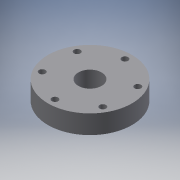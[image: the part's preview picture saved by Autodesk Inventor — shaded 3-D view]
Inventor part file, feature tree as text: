
AUTODESK INVENTOR PART (.ipt)
format: ipt  version: 2016 (Build 200138000, 138)  size: 130,048 bytes
history: native  units: in
note: dims shown in document units (in); Inventor stores cm internally (conversion verified against a paired STEP export)
features: extrude x1, sketch x1
ambient origin geometry x8: Origin, YZ Plane, XZ Plane, XY Plane, X Axis, Y Axis, Z Axis, Center Point
bodies: Body1 (feature_tree)
feature tree (2):
  extrude  "Extrusion2"  Depth=0.503in
  sketch  "Sketch1"  dims[d0=1.875in d1=0.17in d2=0.17in d3=0.17in d4=0.17in d5=0.17in d6=0.17in d7=2.25in d10=0.625in d11=0.503in d12=0.0in]
